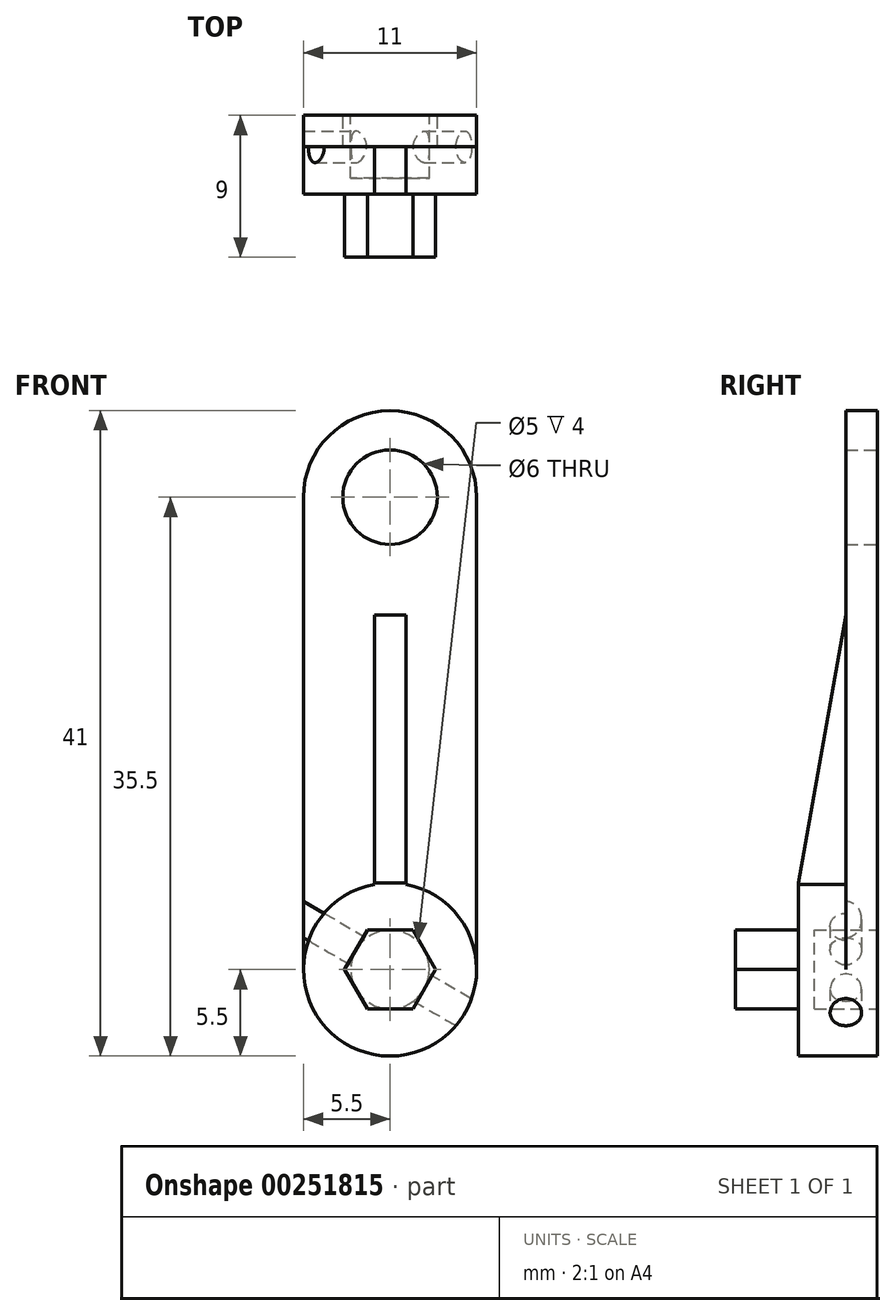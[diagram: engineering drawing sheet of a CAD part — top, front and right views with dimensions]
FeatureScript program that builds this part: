
annotation { "Feature Type Name" : "Feature", "Feature Type Description" : "" }
export const myFeature = defineFeature(function(context is Context, id is Id, definition is map)
    precondition{}
    {
        {
            var Q0;
            Q0=qCreatedBy(makeId("Front.planeOp"),FACE);
            var sketch = newSketch(context, id + "F0", { "sketchPlane" : qUnion([Q0])});
            skCircle(sketch, "E0", {"center": v(0, 0) * mm, "radius": 5.5 * mm});
            skLineSegment(sketch, "E1", {"start": v(-14.1, 0) * mm, "end": v(17.82, 0) * mm, "construction": true});
            skLineSegment(sketch, "E2", {"start": v(-7.8, 30) * mm, "end": v(7.8, 30) * mm, "construction": true});
            skLineSegment(sketch, "E3", {"start": v(0, -12.88) * mm, "end": v(0, 59.28) * mm, "construction": true});
            skArc(sketch, "E4", {"start": v(5.5, 30) * mm, "mid": v(0, 35.5) * mm, "end": v(-5.5, 30) * mm});
            skLineSegment(sketch, "E5", {"start": v(-5.5, 30) * mm, "end": v(-5.5, 0) * mm});
            skLineSegment(sketch, "E6.MirrorCS", {"start": v(5.5, 30) * mm, "end": v(5.5, 0) * mm});
            skCircle(sketch, "E7", {"center": v(0, 30) * mm, "radius": 3 * mm});
            skCircle(sketch, "E8.cCircle", {"center": v(0, 0) * mm, "radius": 2.5 * mm, "construction": true});
            skLineSegment(sketch, "E8.0", {"start": v(1.44, -2.5) * mm, "end": v(-1.44, -2.5) * mm});
            skLineSegment(sketch, "E8.1", {"start": v(-1.44, -2.5) * mm, "end": v(-2.89, 0) * mm});
            skLineSegment(sketch, "E8.2", {"start": v(-2.89, 0) * mm, "end": v(-1.44, 2.5) * mm});
            skLineSegment(sketch, "E8.3", {"start": v(-1.44, 2.5) * mm, "end": v(1.44, 2.5) * mm});
            skLineSegment(sketch, "E8.4", {"start": v(1.44, 2.5) * mm, "end": v(2.89, 0) * mm});
            skLineSegment(sketch, "E8.5", {"start": v(2.89, 0) * mm, "end": v(1.44, -2.5) * mm});
            skPoint(sketch, "E8.0.midPoint", {"position": v(0, -2.5) * mm});
            skLineSegment(sketch, "E9", {"start": v(-12.6, 8.03) * mm, "end": v(10.94, -6.97) * mm, "construction": true});
            skSolve(sketch);
        }
        {
            var Q0;
            Q0=makeQuery(id+"F0.imprint","IMPRINT",FACE,{"disambiguationData":[TD([[makeQuery(id+"F0.imprint","IMPRINT",EDGE,{"derivedFrom":sQuery(id+"F0.wireOp",EDGE,"E4")}),1.0]])]});
            extrude(context, id + "F1", {"entities" : qUnion([Q0]), "depth" : 2 * mm});
        }
        {
            var Q0;
            Q0=makeQuery(id+"F0.imprint","IMPRINT",FACE,{"disambiguationData":[TD([[makeQuery(id+"F0.imprint","IMPRINT",EDGE,{"derivedFrom":sQuery(id+"F0.wireOp",EDGE,"E8.0")}),1.0]])]});
            extrude(context, id + "F2", {"entities" : qUnion([Q0]), "operationType" : NewBodyOperationType.ADD, "depth" : 5 * mm});
        }
        {
            var Q0;
            Q0=makeQuery(id+"F0.imprint","IMPRINT",FACE,{"disambiguationData":[TD([[makeQuery(id+"F0.imprint","IMPRINT",EDGE,{"derivedFrom":sQuery(id+"F0.wireOp",EDGE,"E8.0")}),-1.0]])]});
            extrude(context, id + "F3", {"entities" : qUnion([Q0]), "operationType" : NewBodyOperationType.ADD, "depth" : 9 * mm});
        }
        {
            var Q0;
            Q0=makeQuery(id+"F0.imprint","IMPRINT",FACE,{"disambiguationData":[TD([[makeQuery(id+"F0.imprint","IMPRINT",EDGE,{"derivedFrom":sQuery(id+"F0.wireOp",EDGE,"E8.0")}),1.0]])]});
            var sketch = newSketch(context, id + "F4", { "sketchPlane" : qUnion([Q0])});
            skCircle(sketch, "E10", {"center": v(0, 0) * mm, "radius": 2.5 * mm});
            skSolve(sketch);
        }
        {
            var Q0;
            Q0 = qSketchRegion(id + "F4", true);
            extrude(context, id + "F5", {"entities" : qUnion([Q0]), "operationType" : NewBodyOperationType.REMOVE, "depth" : 4 * mm});
        }
        {
            var Q0;
            Q0=qCreatedBy(makeId("Right.planeOp"),FACE);
            var sketch = newSketch(context, id + "F6", { "sketchPlane" : qUnion([Q0])});
            skLineSegment(sketch, "E11.0", {"start": v(-5, 3.94) * mm, "end": v(-5, 5.5) * mm});
            skLineSegment(sketch, "E12", {"start": v(-5, 3.94) * mm, "end": v(0, 3.94) * mm});
            skPoint(sketch, "E13.orphan", {"position": v(-5, -5.5) * mm});
            skLineSegment(sketch, "E14", {"start": v(-5, 5.5) * mm, "end": v(-1.73, 24.02) * mm});
            skLineSegment(sketch, "E15", {"start": v(0, 3.94) * mm, "end": v(0, 23.93) * mm});
            skLineSegment(sketch, "E16", {"start": v(0, 23.93) * mm, "end": v(-1.73, 24.02) * mm});
            skSolve(sketch);
        }
        {
            var Q0;
            Q0=makeQuery(id+"F6.imprint","IMPRINT",FACE,{"disambiguationData":[TD([[makeQuery(id+"F6.imprint","IMPRINT",EDGE,{"derivedFrom":sQuery(id+"F6.wireOp",EDGE,"E11.0")}),-1.0]])]});
            extrude(context, id + "F7", {"entities" : qUnion([Q0]), "operationType" : NewBodyOperationType.ADD, "endBound" : BoundingType.SYMMETRIC, "depth" : 2 * mm});
        }
        {
            var Q0;
            Q0=makeQuery(id+"F3.opExtrude","SWEPT_FACE",FACE,{"disambiguationData":[OSD([sQuery(id+"F0.wireOp",EDGE,"E8.5")])]});
            cPlane(context, id + "F8", {"entities" : qUnion([Q0]), "cplaneType" : CPlaneType.OFFSET, "offset" : 3 * mm, "width" : 150 * mm, "height" : 150 * mm});
        }
        {
            var Q0;
            Q0=qCreatedBy(id+"F8.planeOp",FACE);
            var sketch = newSketch(context, id + "F9", { "sketchPlane" : qUnion([Q0])});
            skPoint(sketch, "E17", {"position": v(-2, 0) * mm});
            skSolve(sketch);
        }
        {
            var Q0;
            Q0=sQuery(id+"F9.wireOp",VERTEX,"E17");
            var Q1;
            Q1=makeQuery(id+"F1.opExtrude","SWEPT_BODY",BODY,{"disambiguationData":[OSD([sQuery(id+"F0.wireOp",EDGE,"E0"),sQuery(id+"F0.wireOp",EDGE,"E4"),sQuery(id+"F0.wireOp",EDGE,"E5"),sQuery(id+"F0.wireOp",EDGE,"E6.MirrorCS"),sQuery(id+"F0.wireOp",EDGE,"E7")])]});
            hole(context, id + "F10", {"style" : HoleStyle.SIMPLE, "endStyle" : HoleEndStyle.THROUGH, "holeDiameter" : 2 * mm, "tappedDepth" : 12 * mm, "tapClearance" : 3, "locations" : qUnion([Q0]), "scope" : qUnion([Q1])});
        }
    });
